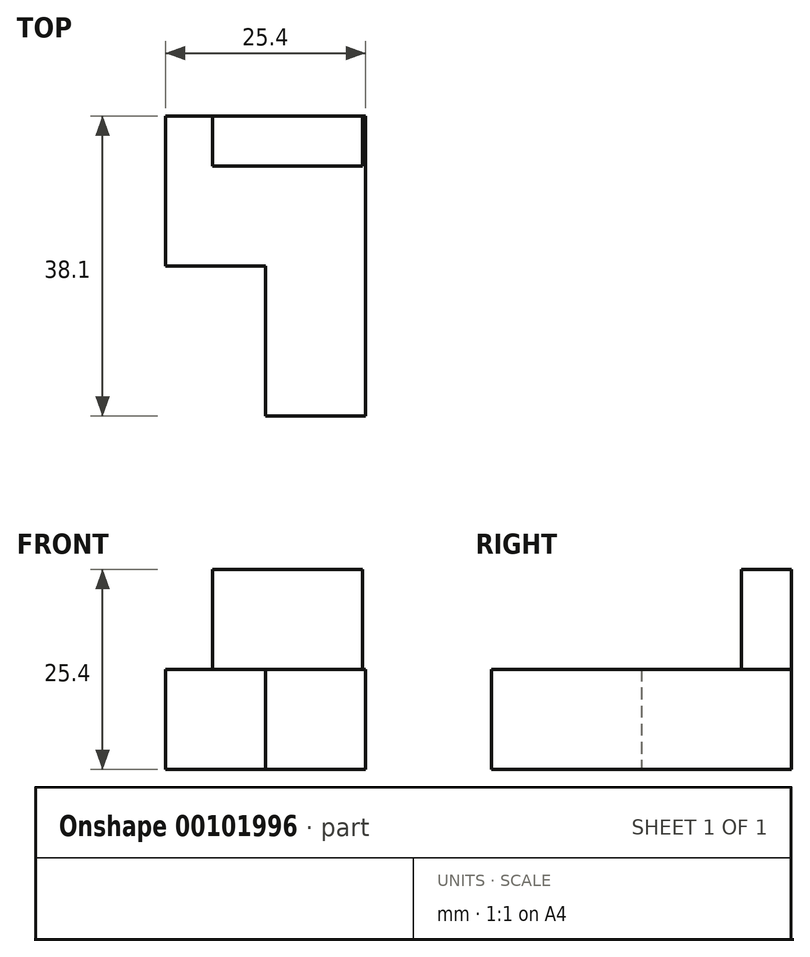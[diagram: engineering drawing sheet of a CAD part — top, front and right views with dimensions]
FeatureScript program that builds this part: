
annotation { "Feature Type Name" : "Feature", "Feature Type Description" : "" }
export const myFeature = defineFeature(function(context is Context, id is Id, definition is map)
    precondition{}
    {
        {
            var Q0;
            Q0=qCreatedBy(makeId("Top.planeOp"),FACE);
            var sketch = newSketch(context, id + "F0", { "sketchPlane" : qUnion([Q0])});
            skLineSegment(sketch, "E0", {"start": v(0, 0) * mm, "end": v(0, -19.05) * mm});
            skLineSegment(sketch, "E1", {"start": v(0, -19.05) * mm, "end": v(12.7, -19.05) * mm});
            skLineSegment(sketch, "E2", {"start": v(12.7, -19.05) * mm, "end": v(12.7, -38.1) * mm});
            skLineSegment(sketch, "E3", {"start": v(12.7, -38.1) * mm, "end": v(25.4, -38.1) * mm});
            skLineSegment(sketch, "E4", {"start": v(25.4, -38.1) * mm, "end": v(25.4, 0) * mm});
            skLineSegment(sketch, "E5", {"start": v(25.4, 0) * mm, "end": v(0, 0) * mm});
            skSolve(sketch);
        }
        {
            var Q0;
            Q0=makeQuery(id+"F0.imprint","IMPRINT",FACE,{"disambiguationData":[TD([[makeQuery(id+"F0.imprint","IMPRINT",EDGE,{"derivedFrom":sQuery(id+"F0.wireOp",EDGE,"E0")}),1.0]])]});
            extrude(context, id + "F1", {"entities" : qUnion([Q0]), "depth" : 12.7 * mm});
        }
        {
            var Q0;
            Q0=qCreatedBy(makeId("Top.planeOp"),FACE);
            var sketch = newSketch(context, id + "F2", { "sketchPlane" : qUnion([Q0])});
            skLineSegment(sketch, "E6", {"start": v(25.01, 0) * mm, "end": v(25.01, -6.35) * mm});
            skLineSegment(sketch, "E7", {"start": v(25.01, -6.35) * mm, "end": v(5.96, -6.35) * mm});
            skLineSegment(sketch, "E8", {"start": v(5.96, -6.35) * mm, "end": v(5.96, 0) * mm});
            skLineSegment(sketch, "E9", {"start": v(5.96, 0) * mm, "end": v(25.01, 0) * mm});
            skSolve(sketch);
        }
        {
            var Q0;
            Q0 = qSketchRegion(id + "F2", true);
            extrude(context, id + "F3", {"entities" : qUnion([Q0]), "operationType" : NewBodyOperationType.ADD, "depth" : 25.4 * mm});
        }
    });
